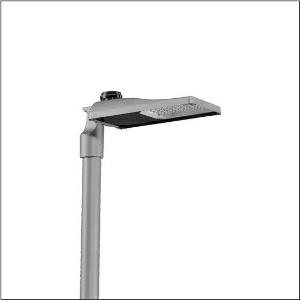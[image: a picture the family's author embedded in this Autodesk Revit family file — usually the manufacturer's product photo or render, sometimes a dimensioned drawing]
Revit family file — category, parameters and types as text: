
# Revit family: streetlight_sl_31_mini___st1_0a_5xh2d3bn08ga_9766
name_source: partatom
category: Lighting Fixtures
units: mm (PartAtom-declared; Revit-internal decimal feet)

## family parameters
Cut with Voids When Loaded = No
Host = Face
Light Source = No
Part Type = Normal
Room Calculation Point = No
Round Connector Dimension = Use Diameter
Shared = No

## types (1)
- --- (1 x LED, 5710 lm, 37.3 W, 3000K)
    Apparent Load = 37 VA
    CIE Flux Codes = 37 72 97 100 100
    Color Rendering = 70
    Color Temperature = 3000K
    Default Elevation = 1800 mm
    Description = Streetlight SL 31 mini NEMA (7pin) mast luminaire for post-top, side-entry; light control with lens of PMMA; light distribution: ST1.0a, direct asymmetric distribution, for standard-compliant lighting for roads and squares; LED: luminous flux: 5.710lm, light colour: 730, colour temperature: 3000K; luminous efficacy: 153,1lm/W; control: overheat protection, intelligent temperature release in ECG and LED module, constant luminous flux control, time-dependent luminous flux control, flexible luminous flux parameterisation, pre-setting: linear dimming characteristic; luminaire housing, of diecast aluminium, Siteco® metallic grey (DB 702S), corrosivity category C5 high according to DIN EN ISO 12944; cover of toughened safety glass, transparent, mast flange of diecast aluminium, Siteco® metallic grey (DB 702S), spigot size: 76/60mm, mast flange included unmounted; with cable H07RN-F 3x 1.5mm², cable length: 6,5m, connection cable pre-assembled; mains connection: 220..240V, AC, 50/60Hz; power consumption (at start of service life): 37,3W / (at end of service life): 38,7W / (with reduced operation 50%): 17,5W; protection rating (complete): IP66; insulation class (complete): insulation class I (protective earthing); impact resistance: IK10; certification: CE, ENEC, ENEC+, VDE, UKCA; permissible operating ambient temperature for outdoor applications: -40..+50°C; packaging unit: 1 piece

Light Distribution: ST1.0a
    Height = 76 mm
    Lamp = 1 x LED
    Lamp Light Flux = 5710 lm
    Lamp Power = 37.3 W
    Lamp count = 1
    Length = 547 mm
    Luminous efficacy = 153 lm/W
    Manufacturer = Siteco
    ModVariant = No
    Model = 5XH2D3BN08GA
    Number of Poles = 1
    OnlyDefault = Yes
    Power Factor = 1
    Product Name = Streetlight SL 31 mini | ST1.0a
    Product group = mast luminaire | pylon top
    ProductGroupID = 6100
    Protection Class = Protection class I
    Protection Degree = IP 66
    RLX_Detail_Level = 1
    RLX_Emergency_Light_Flux = 0 lm
    RLX_Emergency_Type = 0
    RLX_Emergency_Type_DB = No
    RlxData = <blob elided: 40017 chars, md5=32d2fd63>
    Socket = socket
    Standby Power = 0 W
    System Light Flux = 5710 lm
    System Power = 37 W
    Type Comments = factory setting: luminous flux: 100 % | dim-lin: 254 | 386 mA
    Type Image = l_1300322.jpg
    URL = http://relux.com
    VarID = @adj_074975
    Voltage = 0 V
    Weight = 0.00 kg
    Width = 265 mm

## geometry (parser evidence)
native form markers: Blend x4, Sweep x8
no freeform markers — native parametric forms only
